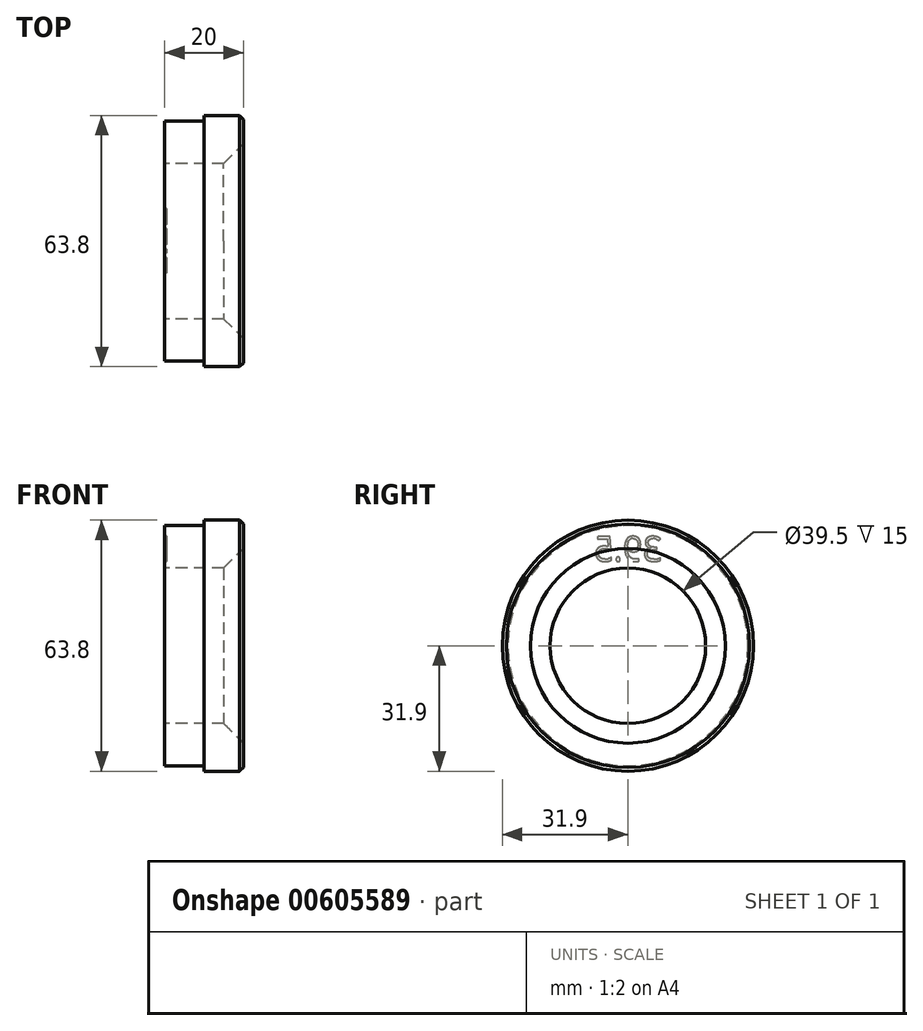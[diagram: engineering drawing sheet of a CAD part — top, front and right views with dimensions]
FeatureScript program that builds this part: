
annotation { "Feature Type Name" : "Feature", "Feature Type Description" : "" }
export const myFeature = defineFeature(function(context is Context, id is Id, definition is map)
    precondition{}
    {
        {
            var Q0;
            Q0=qCreatedBy(makeId("Front.planeOp"),FACE);
            var sketch = newSketch(context, id + "F0", { "sketchPlane" : qUnion([Q0])});
            skLineSegment(sketch, "E0", {"start": v(0, 0) * mm, "end": v(45.1, 0) * mm, "construction": true});
            skLineSegment(sketch, "E1", {"start": v(0, 19.75) * mm, "end": v(0, 30.5) * mm});
            skLineSegment(sketch, "E2", {"start": v(0, 30.5) * mm, "end": v(10, 30.5) * mm});
            skLineSegment(sketch, "E3", {"start": v(10, 30.5) * mm, "end": v(10, 31.9) * mm});
            skLineSegment(sketch, "E4", {"start": v(10, 31.9) * mm, "end": v(20, 31.9) * mm});
            skLineSegment(sketch, "E5", {"start": v(20, 31.9) * mm, "end": v(20, 19.75) * mm});
            skLineSegment(sketch, "E6", {"start": v(20, 19.75) * mm, "end": v(0, 19.75) * mm});
            skSolve(sketch);
        }
        {
            var Q0;
            Q0=qSketchRegion(id+"F0",true);
            var Q1;
            Q1=sQuery(id+"F0.wireOp",EDGE,"E0");
            revolve(context, id + "F1", {"entities" : qUnion([Q0]), "axis" : qUnion([Q1]), "revolveType" : RevolveType.FULL});
        }
        {
            var Q0;
            Q0=makeQuery(id+"F1.opRevolve","SWEPT_EDGE",EDGE,{"disambiguationData":[OSD([sQuery(id+"F0.wireOp",EDGE,"E4"),sQuery(id+"F0.wireOp",EDGE,"E5")])]});
            chamfer(context, id + "F2", {"entities" : qUnion([Q0]), "width" : 1 * mm, "tangentPropagation" : true});
        }
        {
            var Q0;
            Q0=makeQuery(id+"F1.opRevolve","SWEPT_EDGE",EDGE,{"disambiguationData":[OSD([sQuery(id+"F0.wireOp",EDGE,"E5"),sQuery(id+"F0.wireOp",EDGE,"E6")])]});
            chamfer(context, id + "F3", {"entities" : qUnion([Q0]), "width" : 5 * mm, "tangentPropagation" : true});
        }
        {
            var Q0;
            Q0=makeQuery(id+"F1.opRevolve","SWEPT_FACE",FACE,{"disambiguationData":[OSD([sQuery(id+"F0.wireOp",EDGE,"E1")])]});
            var sketch = newSketch(context, id + "F4", { "sketchPlane" : qUnion([Q0])});
            skText(sketch, "E7", { "text": "39.5", "fontName": "OpenSans-Regular.ttf"});
            skLineSegment(sketch, "E8", {"start": v(0, 0) * mm, "end": v(0, 30.5) * mm, "construction": true});
            const initialGuessF4  = {"E7": [-0.00873, 0.02149, 1, 0, 0.00632]};
            skSetInitialGuess(sketch, initialGuessF4);
            skSolve(sketch);
        }
        {
            var Q0;
            Q0 = qSketchRegion(id + "F4", true);
            extrude(context, id + "F5", {"entities" : qUnion([Q0]), "operationType" : NewBodyOperationType.REMOVE, "oppositeDirection" : true, "depth" : 0.5 * mm, "offsetDistance" : 25 * mm});
        }
    });
